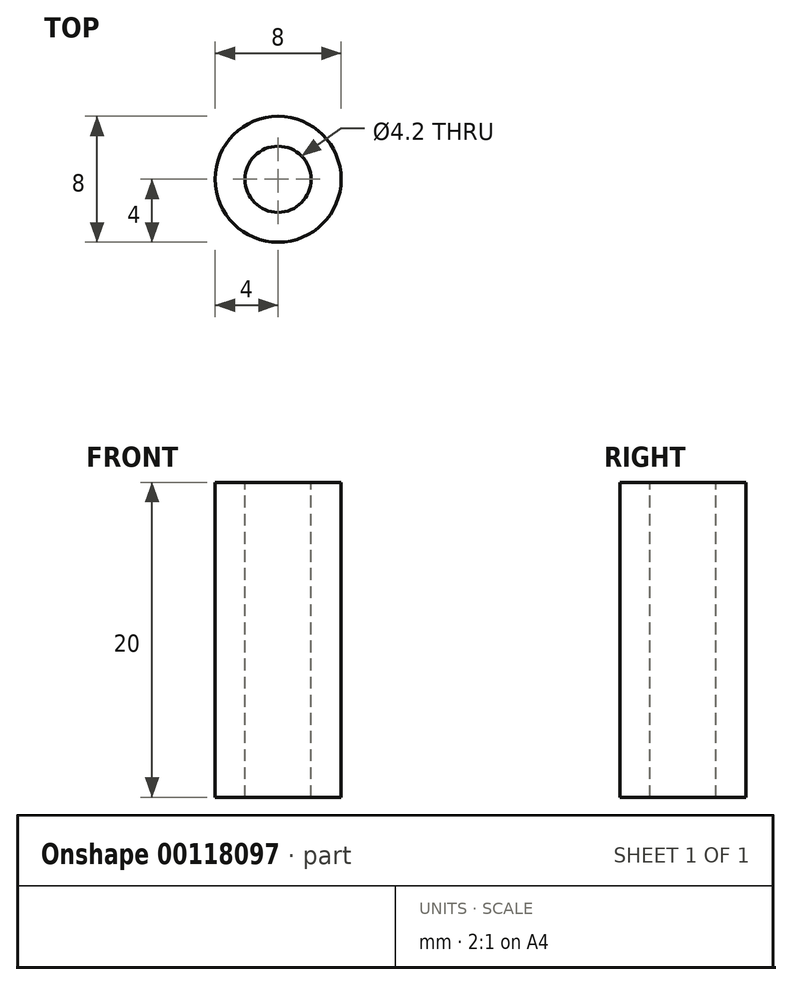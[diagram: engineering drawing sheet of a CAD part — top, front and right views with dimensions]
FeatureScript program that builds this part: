
annotation { "Feature Type Name" : "Feature", "Feature Type Description" : "" }
export const myFeature = defineFeature(function(context is Context, id is Id, definition is map)
    precondition{}
    {
        {
            var Q0;
            Q0=qCreatedBy(makeId("Top.planeOp"),FACE);
            var sketch = newSketch(context, id + "F0", { "sketchPlane" : qUnion([Q0])});
            skCircle(sketch, "E0", {"center": v(0, 0) * mm, "radius": 4 * mm});
            skSolve(sketch);
        }
        {
            var Q0;
            Q0=makeQuery(id+"F0.imprint","IMPRINT",FACE,{"disambiguationData":[TD([[makeQuery(id+"F0.imprint","IMPRINT",EDGE,{"derivedFrom":sQuery(id+"F0.wireOp",EDGE,"E0")}),1.0]])]});
            extrude(context, id + "F1", {"entities" : qUnion([Q0]), "endBound" : BoundingType.SYMMETRIC, "depth" : 20 * mm});
        }
        {
            var Q0;
            Q0=makeQuery(id+"F1.opExtrude","CAP_FACE",FACE,{"disambiguationData":[OSD([sQuery(id+"F0.wireOp",EDGE,"E0")])],"isStart":false});
            var sketch = newSketch(context, id + "F2", { "sketchPlane" : qUnion([Q0])});
            skPoint(sketch, "E1", {"position": v(0, 0) * mm});
            skSolve(sketch);
        }
        {
            var Q0;
            Q0=sQuery(id+"F2.wireOp",VERTEX,"E1");
            var Q1;
            Q1=makeQuery(id+"F1.opExtrude","SWEPT_BODY",BODY,{"disambiguationData":[OSD([sQuery(id+"F0.wireOp",EDGE,"E0")])]});
            hole(context, id + "F3", {"style" : HoleStyle.SIMPLE, "endStyle" : HoleEndStyle.THROUGH, "standardTappedOrClearance" : lookupTablePath({ "standard" : "ISO", "engagement" : "75%", "pitch" : "0.8 mm", "size" : "M5", "type" : "Tapped" }), "standardBlindInLast" : lookupTablePath({ "standard" : "ISO", "engagement" : "75%", "pitch" : "0.8 mm", "size" : "M5", "type" : "Tapped" }), "holeDiameter" : 4.2 * mm, "startFromSketch" : true, "locations" : qUnion([Q0]), "scope" : qUnion([Q1]), "isTappedThrough" : true, "majorDiameter" : 5 * mm, "showTappedDepth" : true});
        }
    });
